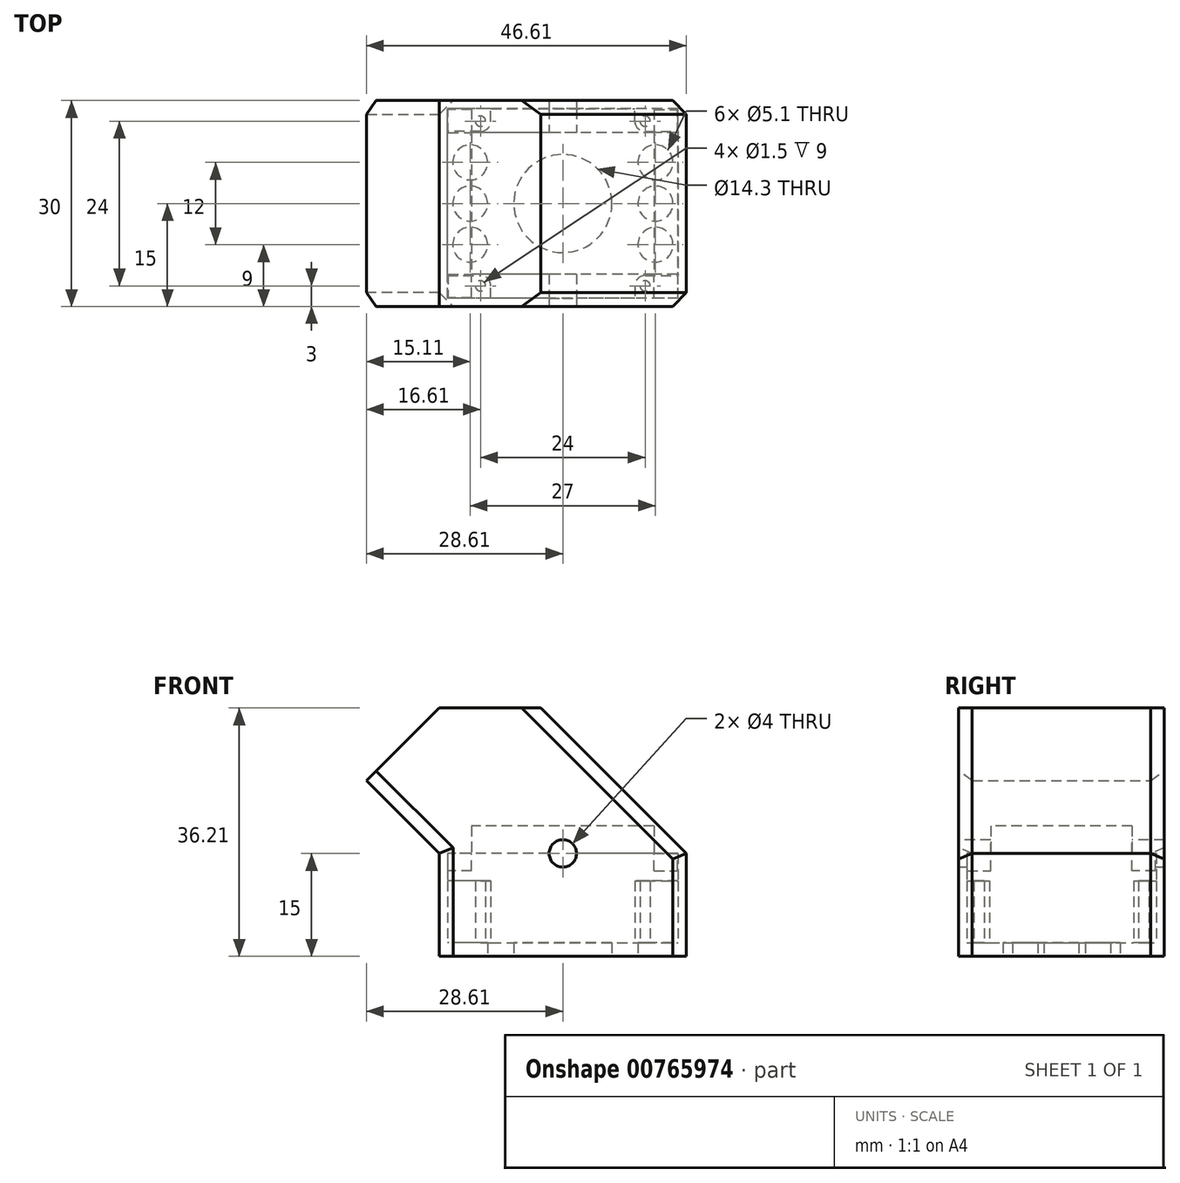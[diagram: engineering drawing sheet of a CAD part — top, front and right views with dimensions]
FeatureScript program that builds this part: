
annotation { "Feature Type Name" : "Feature", "Feature Type Description" : "" }
export const myFeature = defineFeature(function(context is Context, id is Id, definition is map)
    precondition{}
    {
        {
            var Q0;
            Q0=qCreatedBy(makeId("Top.planeOp"),FACE);
            var sketch = newSketch(context, id + "F0", { "sketchPlane" : qUnion([Q0])});
            skLineSegment(sketch, "E0.bottom", {"start": v(12, -12) * mm, "end": v(-12, -12) * mm, "construction": true});
            skLineSegment(sketch, "E0.top", {"start": v(12, 12) * mm, "end": v(-12, 12) * mm, "construction": true});
            skLineSegment(sketch, "E0.left", {"start": v(12, -12) * mm, "end": v(12, 12) * mm, "construction": true});
            skLineSegment(sketch, "E0.right", {"start": v(-12, -12) * mm, "end": v(-12, 12) * mm, "construction": true});
            skPoint(sketch, "E0.middle", {"position": v(0, 0) * mm});
            skCircle(sketch, "E1", {"center": v(-12, 12) * mm, "radius": 0.75 * mm});
            skCircle(sketch, "E2", {"center": v(-12, -12) * mm, "radius": 0.75 * mm});
            skCircle(sketch, "E3", {"center": v(12, -12) * mm, "radius": 0.75 * mm});
            skCircle(sketch, "E4", {"center": v(12, 12) * mm, "radius": 0.75 * mm});
            skCircle(sketch, "E5", {"center": v(0, 0) * mm, "radius": 7.15 * mm});
            skLineSegment(sketch, "E6", {"start": v(-13.5, 6) * mm, "end": v(-13.5, -6) * mm, "construction": true});
            skLineSegment(sketch, "E7", {"start": v(13.5, 6) * mm, "end": v(13.5, -6) * mm, "construction": true});
            skCircle(sketch, "E8", {"center": v(-13.5, 6) * mm, "radius": 2.55 * mm});
            skCircle(sketch, "E9", {"center": v(-13.5, 0) * mm, "radius": 2.55 * mm});
            skCircle(sketch, "E10", {"center": v(-13.5, -6) * mm, "radius": 2.55 * mm});
            skCircle(sketch, "E11", {"center": v(13.5, -6) * mm, "radius": 2.55 * mm});
            skCircle(sketch, "E12", {"center": v(13.5, 0) * mm, "radius": 2.55 * mm});
            skCircle(sketch, "E13", {"center": v(13.5, 6) * mm, "radius": 2.55 * mm});
            skLineSegment(sketch, "E14.bottom", {"start": v(15, -12.5) * mm, "end": v(-15, -12.5) * mm});
            skLineSegment(sketch, "E14.top", {"start": v(15, 12.5) * mm, "end": v(-15, 12.5) * mm});
            skLineSegment(sketch, "E14.left", {"start": v(15, -12.5) * mm, "end": v(15, 12.5) * mm});
            skLineSegment(sketch, "E14.right", {"start": v(-15, -12.5) * mm, "end": v(-15, 12.5) * mm});
            skSolve(sketch);
        }
        {
            var Q0;
            Q0=qCreatedBy(makeId("Top.planeOp"),FACE);
            var sketch = newSketch(context, id + "F1", { "sketchPlane" : qUnion([Q0])});
            skLineSegment(sketch, "E15.bottom", {"start": v(18, -15) * mm, "end": v(-18, -15) * mm});
            skLineSegment(sketch, "E15.top", {"start": v(18, 15) * mm, "end": v(-18, 15) * mm});
            skLineSegment(sketch, "E15.left", {"start": v(18, -15) * mm, "end": v(18, 15) * mm});
            skLineSegment(sketch, "E15.right", {"start": v(-18, -15) * mm, "end": v(-18, 15) * mm});
            skPoint(sketch, "E15.middle", {"position": v(0, 0) * mm});
            skCircle(sketch, "E16", {"center": v(0, 0) * mm, "radius": 7.15 * mm});
            skCircle(sketch, "E17", {"center": v(-13.5, 6) * mm, "radius": 2.55 * mm});
            skCircle(sketch, "E18", {"center": v(-13.5, 0) * mm, "radius": 2.55 * mm});
            skCircle(sketch, "E19", {"center": v(-13.5, -6) * mm, "radius": 2.55 * mm});
            skCircle(sketch, "E20", {"center": v(13.5, 6) * mm, "radius": 2.55 * mm});
            skCircle(sketch, "E21", {"center": v(13.5, 0) * mm, "radius": 2.55 * mm});
            skCircle(sketch, "E22", {"center": v(13.5, -6) * mm, "radius": 2.55 * mm});
            skSolve(sketch);
        }
        {
            var Q0;
            Q0=qSketchRegion(id+"F1",true);
            extrude(context, id + "F2", {"entities" : qUnion([Q0]), "depth" : 2 * mm, "offsetDistance" : 25 * mm});
        }
        {
            var Q0;
            Q0=makeQuery(id+"F2.opExtrude","CAP_FACE",FACE,{"disambiguationData":[OSD([sQuery(id+"F1.wireOp",EDGE,"E15.bottom"),sQuery(id+"F1.wireOp",EDGE,"E15.top"),sQuery(id+"F1.wireOp",EDGE,"E15.left"),sQuery(id+"F1.wireOp",EDGE,"E15.right"),sQuery(id+"F1.wireOp",EDGE,"E16"),sQuery(id+"F1.wireOp",EDGE,"E17"),sQuery(id+"F1.wireOp",EDGE,"E18"),sQuery(id+"F1.wireOp",EDGE,"E19"),sQuery(id+"F1.wireOp",EDGE,"E20"),sQuery(id+"F1.wireOp",EDGE,"E21"),sQuery(id+"F1.wireOp",EDGE,"E22")])],"isStart":false});
            var sketch = newSketch(context, id + "F3", { "sketchPlane" : qUnion([Q0])});
            skLineSegment(sketch, "E23.bottom", {"start": v(18, -15) * mm, "end": v(-18, -15) * mm});
            skLineSegment(sketch, "E23.top", {"start": v(18, 15) * mm, "end": v(-18, 15) * mm});
            skLineSegment(sketch, "E23.left", {"start": v(18, -15) * mm, "end": v(18, 15) * mm});
            skLineSegment(sketch, "E23.right", {"start": v(-18, -15) * mm, "end": v(-18, 15) * mm});
            skPoint(sketch, "E23.middle", {"position": v(0, 0) * mm});
            skLineSegment(sketch, "E24", {"start": v(-12, 10.5) * mm, "end": v(-16.8, 10.5) * mm});
            skLineSegment(sketch, "E25", {"start": v(-10.5, 12) * mm, "end": v(-10.5, 13.8) * mm});
            skLineSegment(sketch, "E26", {"start": v(-10.5, -13.8) * mm, "end": v(-10.5, -12) * mm});
            skLineSegment(sketch, "E27", {"start": v(-16.8, -10.5) * mm, "end": v(-12, -10.5) * mm});
            skLineSegment(sketch, "E28", {"start": v(10.5, -12) * mm, "end": v(10.5, -13.8) * mm});
            skLineSegment(sketch, "E29", {"start": v(12, -10.5) * mm, "end": v(16.8, -10.5) * mm});
            skLineSegment(sketch, "E30", {"start": v(10.5, 12) * mm, "end": v(10.5, 13.8) * mm});
            skLineSegment(sketch, "E31", {"start": v(12, 10.5) * mm, "end": v(16.8, 10.5) * mm});
            skArc(sketch, "E32", {"start": v(-12, 10.5) * mm, "mid": v(-10.94, 10.94) * mm, "end": v(-10.5, 12) * mm});
            skArc(sketch, "E33", {"start": v(10.5, 12) * mm, "mid": v(10.94, 10.94) * mm, "end": v(12, 10.5) * mm});
            skArc(sketch, "E34", {"start": v(12, -10.5) * mm, "mid": v(10.94, -10.94) * mm, "end": v(10.5, -12) * mm});
            skArc(sketch, "E35", {"start": v(-10.5, -12) * mm, "mid": v(-10.94, -10.94) * mm, "end": v(-12, -10.5) * mm});
            skLineSegment(sketch, "E36", {"start": v(-10.5, 13.8) * mm, "end": v(10.5, 13.8) * mm});
            skLineSegment(sketch, "E37", {"start": v(16.8, 10.5) * mm, "end": v(16.8, -10.5) * mm});
            skLineSegment(sketch, "E38", {"start": v(10.5, -13.8) * mm, "end": v(-10.5, -13.8) * mm});
            skLineSegment(sketch, "E39", {"start": v(-16.8, -10.5) * mm, "end": v(-16.8, 10.5) * mm});
            skCircle(sketch, "E40", {"center": v(-12, 12) * mm, "radius": 0.75 * mm});
            skCircle(sketch, "E41", {"center": v(12, 12) * mm, "radius": 0.75 * mm});
            skCircle(sketch, "E42", {"center": v(12, -12) * mm, "radius": 0.75 * mm});
            skCircle(sketch, "E43", {"center": v(-12, -12) * mm, "radius": 0.75 * mm});
            skSolve(sketch);
        }
        {
            var Q0;
            Q0=qSketchRegion(id+"F3",true);
            extrude(context, id + "F4", {"entities" : qUnion([Q0]), "operationType" : NewBodyOperationType.ADD, "depth" : 9 * mm, "offsetDistance" : 25 * mm});
        }
        {
            var Q0;
            Q0=makeQuery(id+"F4.opExtrude","CAP_FACE",FACE,{"disambiguationData":[OSD([sQuery(id+"F3.wireOp",EDGE,"E23.bottom"),sQuery(id+"F3.wireOp",EDGE,"E23.top"),sQuery(id+"F3.wireOp",EDGE,"E23.left"),sQuery(id+"F3.wireOp",EDGE,"E23.right"),sQuery(id+"F3.wireOp",EDGE,"E24"),sQuery(id+"F3.wireOp",EDGE,"E25"),sQuery(id+"F3.wireOp",EDGE,"E26"),sQuery(id+"F3.wireOp",EDGE,"E27"),sQuery(id+"F3.wireOp",EDGE,"E28"),sQuery(id+"F3.wireOp",EDGE,"E29"),sQuery(id+"F3.wireOp",EDGE,"E30"),sQuery(id+"F3.wireOp",EDGE,"E31"),sQuery(id+"F3.wireOp",EDGE,"E32"),sQuery(id+"F3.wireOp",EDGE,"E33"),sQuery(id+"F3.wireOp",EDGE,"E34"),sQuery(id+"F3.wireOp",EDGE,"E35"),sQuery(id+"F3.wireOp",EDGE,"E36"),sQuery(id+"F3.wireOp",EDGE,"E37"),sQuery(id+"F3.wireOp",EDGE,"E38"),sQuery(id+"F3.wireOp",EDGE,"E39"),sQuery(id+"F3.wireOp",EDGE,"E40"),sQuery(id+"F3.wireOp",EDGE,"E41"),sQuery(id+"F3.wireOp",EDGE,"E42"),sQuery(id+"F3.wireOp",EDGE,"E43")])],"isStart":false});
            var sketch = newSketch(context, id + "F5", { "sketchPlane" : qUnion([Q0])});
            skLineSegment(sketch, "E44.bottom", {"start": v(18, -15) * mm, "end": v(-18, -15) * mm});
            skLineSegment(sketch, "E44.top", {"start": v(18, 15) * mm, "end": v(-18, 15) * mm});
            skLineSegment(sketch, "E44.left", {"start": v(18, -15) * mm, "end": v(18, 15) * mm});
            skLineSegment(sketch, "E44.right", {"start": v(-18, -15) * mm, "end": v(-18, 15) * mm});
            skPoint(sketch, "E44.middle", {"position": v(0, 0) * mm});
            skLineSegment(sketch, "E45.bottom", {"start": v(16.8, -13.8) * mm, "end": v(-16.8, -13.8) * mm});
            skLineSegment(sketch, "E45.top", {"start": v(16.8, 13.8) * mm, "end": v(-16.8, 13.8) * mm});
            skLineSegment(sketch, "E45.left", {"start": v(16.8, -13.8) * mm, "end": v(16.8, 13.8) * mm});
            skLineSegment(sketch, "E45.right", {"start": v(-16.8, -13.8) * mm, "end": v(-16.8, 13.8) * mm});
            skSolve(sketch);
        }
        {
            var Q0;
            Q0=qSketchRegion(id+"F5",true);
            extrude(context, id + "F6", {"entities" : qUnion([Q0]), "operationType" : NewBodyOperationType.ADD, "depth" : 4 * mm, "offsetDistance" : 25 * mm});
        }
        {
            var Q0;
            Q0=makeQuery(id+"F6.opExtrude","CAP_FACE",FACE,{"disambiguationData":[OSD([sQuery(id+"F5.wireOp",EDGE,"E44.bottom"),sQuery(id+"F5.wireOp",EDGE,"E44.top"),sQuery(id+"F5.wireOp",EDGE,"E44.left"),sQuery(id+"F5.wireOp",EDGE,"E44.right"),sQuery(id+"F5.wireOp",EDGE,"E45.bottom"),sQuery(id+"F5.wireOp",EDGE,"E45.top"),sQuery(id+"F5.wireOp",EDGE,"E45.left"),sQuery(id+"F5.wireOp",EDGE,"E45.right")])],"isStart":false});
            var sketch = newSketch(context, id + "F7", { "sketchPlane" : qUnion([Q0])});
            skLineSegment(sketch, "E46.bottom", {"start": v(18, -15) * mm, "end": v(-18, -15) * mm});
            skLineSegment(sketch, "E46.top", {"start": v(18, 15) * mm, "end": v(-18, 15) * mm});
            skLineSegment(sketch, "E46.left", {"start": v(18, -15) * mm, "end": v(18, 15) * mm});
            skLineSegment(sketch, "E46.right", {"start": v(-18, -15) * mm, "end": v(-18, 15) * mm});
            skPoint(sketch, "E46.middle", {"position": v(0, 0) * mm});
            skLineSegment(sketch, "E47.top", {"start": v(-16.8, 10.3) * mm, "end": v(-13.3, 10.3) * mm});
            skLineSegment(sketch, "E47.right", {"start": v(-13.3, 13.8) * mm, "end": v(-13.3, 10.3) * mm});
            skLineSegment(sketch, "E48.top", {"start": v(16.8, 10.3) * mm, "end": v(13.3, 10.3) * mm});
            skLineSegment(sketch, "E48.right", {"start": v(13.3, 13.8) * mm, "end": v(13.3, 10.3) * mm});
            skLineSegment(sketch, "E49.top", {"start": v(16.8, -10.3) * mm, "end": v(13.3, -10.3) * mm});
            skLineSegment(sketch, "E49.right", {"start": v(13.3, -13.8) * mm, "end": v(13.3, -10.3) * mm});
            skLineSegment(sketch, "E50.top", {"start": v(-16.8, -10.3) * mm, "end": v(-13.3, -10.3) * mm});
            skLineSegment(sketch, "E50.right", {"start": v(-13.3, -13.8) * mm, "end": v(-13.3, -10.3) * mm});
            skLineSegment(sketch, "E51", {"start": v(-16.8, -10.3) * mm, "end": v(-16.8, 10.3) * mm});
            skLineSegment(sketch, "E52", {"start": v(-13.3, 13.8) * mm, "end": v(13.3, 13.8) * mm});
            skLineSegment(sketch, "E53", {"start": v(16.8, 10.3) * mm, "end": v(16.8, -10.3) * mm});
            skLineSegment(sketch, "E54", {"start": v(13.3, -13.8) * mm, "end": v(-13.3, -13.8) * mm});
            skSolve(sketch);
        }
        {
            var Q0;
            Q0=qSketchRegion(id+"F7",true);
            extrude(context, id + "F8", {"entities" : qUnion([Q0]), "depth" : 4 * mm, "offsetDistance" : 25 * mm});
        }
        {
            var Q0;
            Q0=makeQuery(id+"F8.opExtrude","CAP_FACE",FACE,{"disambiguationData":[OSD([sQuery(id+"F7.wireOp",EDGE,"E46.bottom"),sQuery(id+"F7.wireOp",EDGE,"E46.top"),sQuery(id+"F7.wireOp",EDGE,"E46.left"),sQuery(id+"F7.wireOp",EDGE,"E46.right"),sQuery(id+"F7.wireOp",EDGE,"E47.top"),sQuery(id+"F7.wireOp",EDGE,"E47.right"),sQuery(id+"F7.wireOp",EDGE,"E48.top"),sQuery(id+"F7.wireOp",EDGE,"E48.right"),sQuery(id+"F7.wireOp",EDGE,"E49.top"),sQuery(id+"F7.wireOp",EDGE,"E49.right"),sQuery(id+"F7.wireOp",EDGE,"E50.top"),sQuery(id+"F7.wireOp",EDGE,"E50.right"),sQuery(id+"F7.wireOp",EDGE,"E51"),sQuery(id+"F7.wireOp",EDGE,"E52"),sQuery(id+"F7.wireOp",EDGE,"E53"),sQuery(id+"F7.wireOp",EDGE,"E54")])],"isStart":true});
            var sketch = newSketch(context, id + "F9", { "sketchPlane" : qUnion([Q0])});
            skLineSegment(sketch, "E55.bottom", {"start": v(-13.3, -10.3) * mm, "end": v(-16.72, -10.3) * mm});
            skLineSegment(sketch, "E55.top", {"start": v(-13.3, -13.72) * mm, "end": v(-16.72, -13.72) * mm});
            skLineSegment(sketch, "E55.left", {"start": v(-13.3, -10.3) * mm, "end": v(-13.3, -13.72) * mm});
            skLineSegment(sketch, "E55.right", {"start": v(-16.72, -10.3) * mm, "end": v(-16.72, -13.72) * mm});
            skLineSegment(sketch, "E56.bottom", {"start": v(13.3, -10.3) * mm, "end": v(16.72, -10.3) * mm});
            skLineSegment(sketch, "E56.top", {"start": v(13.3, -13.72) * mm, "end": v(16.72, -13.72) * mm});
            skLineSegment(sketch, "E56.left", {"start": v(13.3, -10.3) * mm, "end": v(13.3, -13.72) * mm});
            skLineSegment(sketch, "E56.right", {"start": v(16.72, -10.3) * mm, "end": v(16.72, -13.72) * mm});
            skLineSegment(sketch, "E57.bottom", {"start": v(-13.3, 10.3) * mm, "end": v(-16.72, 10.3) * mm});
            skLineSegment(sketch, "E57.top", {"start": v(-13.3, 13.72) * mm, "end": v(-16.72, 13.72) * mm});
            skLineSegment(sketch, "E57.left", {"start": v(-13.3, 10.3) * mm, "end": v(-13.3, 13.72) * mm});
            skLineSegment(sketch, "E57.right", {"start": v(-16.72, 10.3) * mm, "end": v(-16.72, 13.72) * mm});
            skLineSegment(sketch, "E58.bottom", {"start": v(13.3, 10.3) * mm, "end": v(16.72, 10.3) * mm});
            skLineSegment(sketch, "E58.top", {"start": v(13.3, 13.72) * mm, "end": v(16.72, 13.72) * mm});
            skLineSegment(sketch, "E58.left", {"start": v(13.3, 10.3) * mm, "end": v(13.3, 13.72) * mm});
            skLineSegment(sketch, "E58.right", {"start": v(16.72, 10.3) * mm, "end": v(16.72, 13.72) * mm});
            skSolve(sketch);
        }
        {
            var Q0;
            Q0=qSketchRegion(id+"F9",true);
            extrude(context, id + "F10", {"entities" : qUnion([Q0]), "operationType" : NewBodyOperationType.ADD, "depth" : 2.5 * mm, "offsetDistance" : 25 * mm});
        }
        {
            var Q0;
            Q0=makeQuery(id+"F8.opExtrude","CAP_FACE",FACE,{"disambiguationData":[OSD([sQuery(id+"F7.wireOp",EDGE,"E46.bottom"),sQuery(id+"F7.wireOp",EDGE,"E46.top"),sQuery(id+"F7.wireOp",EDGE,"E46.left"),sQuery(id+"F7.wireOp",EDGE,"E46.right"),sQuery(id+"F7.wireOp",EDGE,"E47.top"),sQuery(id+"F7.wireOp",EDGE,"E47.right"),sQuery(id+"F7.wireOp",EDGE,"E48.top"),sQuery(id+"F7.wireOp",EDGE,"E48.right"),sQuery(id+"F7.wireOp",EDGE,"E49.top"),sQuery(id+"F7.wireOp",EDGE,"E49.right"),sQuery(id+"F7.wireOp",EDGE,"E50.top"),sQuery(id+"F7.wireOp",EDGE,"E50.right"),sQuery(id+"F7.wireOp",EDGE,"E51"),sQuery(id+"F7.wireOp",EDGE,"E52"),sQuery(id+"F7.wireOp",EDGE,"E53"),sQuery(id+"F7.wireOp",EDGE,"E54")])],"isStart":false});
            var sketch = newSketch(context, id + "F11", { "sketchPlane" : qUnion([Q0])});
            skLineSegment(sketch, "E59.bottom", {"start": v(18, -15) * mm, "end": v(-18, -15) * mm});
            skLineSegment(sketch, "E59.top", {"start": v(18, 15) * mm, "end": v(-18, 15) * mm});
            skLineSegment(sketch, "E59.left", {"start": v(18, -15) * mm, "end": v(18, 15) * mm});
            skLineSegment(sketch, "E59.right", {"start": v(-18, -15) * mm, "end": v(-18, 15) * mm});
            skPoint(sketch, "E59.middle", {"position": v(0, 0) * mm});
            skSolve(sketch);
        }
        {
            var Q0;
            Q0=qSketchRegion(id+"F11",true);
            extrude(context, id + "F12", {"entities" : qUnion([Q0]), "operationType" : NewBodyOperationType.ADD, "depth" : 2 * mm, "offsetDistance" : 25 * mm});
        }
        {
            var Q0;
            Q0=qCreatedBy(makeId("Front.planeOp"),FACE);
            var sketch = newSketch(context, id + "F13", { "sketchPlane" : qUnion([Q0])});
            skLineSegment(sketch, "E60", {"start": v(0, -28.52) * mm, "end": v(-155.56, -184.08) * mm, "construction": true});
            skLineSegment(sketch, "E61", {"start": v(0, -28.52) * mm, "end": v(155.56, -184.08) * mm, "construction": true});
            skLineSegment(sketch, "E62", {"start": v(-10.6, 43.6) * mm, "end": v(22.27, 10.73) * mm, "construction": true});
            skLineSegment(sketch, "E63", {"start": v(-10.6, 43.6) * mm, "end": v(-30.76, 23.45) * mm, "construction": true});
            skLineSegment(sketch, "E64", {"start": v(-18, 36.21) * mm, "end": v(-28.6, 25.6) * mm});
            skLineSegment(sketch, "E65", {"start": v(-28.6, 25.6) * mm, "end": v(-18, 15) * mm});
            skLineSegment(sketch, "E66", {"start": v(-18, 15) * mm, "end": v(18, 15) * mm});
            skLineSegment(sketch, "E67", {"start": v(18, 15) * mm, "end": v(-3.21, 36.21) * mm});
            skLineSegment(sketch, "E68", {"start": v(-3.21, 36.21) * mm, "end": v(-18, 36.21) * mm});
            skSolve(sketch);
        }
        {
            var Q0;
            Q0=qSketchRegion(id+"F13",true);
            extrude(context, id + "F14", {"entities" : qUnion([Q0]), "operationType" : NewBodyOperationType.ADD, "endBound" : BoundingType.SYMMETRIC, "depth" : 30 * mm, "offsetDistance" : 25 * mm});
        }
        {
            var Q0;
            Q0=qCreatedBy(makeId("Front.planeOp"),FACE);
            var sketch = newSketch(context, id + "F15", { "sketchPlane" : qUnion([Q0])});
            skLineSegment(sketch, "E69", {"start": v(12, 21) * mm, "end": v(18, 15) * mm});
            skLineSegment(sketch, "E70", {"start": v(18, 15) * mm, "end": v(18, 21) * mm});
            skLineSegment(sketch, "E71", {"start": v(18, 21) * mm, "end": v(12, 21) * mm});
            skSolve(sketch);
        }
        {
            var Q0;
            Q0=qSketchRegion(id+"F15",true);
            extrude(context, id + "F16", {"entities" : qUnion([Q0]), "operationType" : NewBodyOperationType.REMOVE, "endBound" : BoundingType.SYMMETRIC, "oppositeDirection" : true, "depth" : 36 * mm, "offsetDistance" : 25 * mm});
        }
        {
            var Q0;
            Q0=makeQuery(id+"F14.boolean.opBoolean","MERGE",FACE,{"derivedFrom":[makeQuery(id+"F8.opExtrude","CAP_FACE",FACE,{"disambiguationData":[OSD([sQuery(id+"F7.wireOp",EDGE,"E46.bottom"),sQuery(id+"F7.wireOp",EDGE,"E46.top"),sQuery(id+"F7.wireOp",EDGE,"E46.left"),sQuery(id+"F7.wireOp",EDGE,"E46.right"),sQuery(id+"F7.wireOp",EDGE,"E47.top"),sQuery(id+"F7.wireOp",EDGE,"E47.right"),sQuery(id+"F7.wireOp",EDGE,"E48.top"),sQuery(id+"F7.wireOp",EDGE,"E48.right"),sQuery(id+"F7.wireOp",EDGE,"E49.top"),sQuery(id+"F7.wireOp",EDGE,"E49.right"),sQuery(id+"F7.wireOp",EDGE,"E50.top"),sQuery(id+"F7.wireOp",EDGE,"E50.right"),sQuery(id+"F7.wireOp",EDGE,"E51"),sQuery(id+"F7.wireOp",EDGE,"E52"),sQuery(id+"F7.wireOp",EDGE,"E53"),sQuery(id+"F7.wireOp",EDGE,"E54")])],"isStart":true}),makeQuery(id+"F14.opExtrude","SWEPT_FACE",FACE,{"disambiguationData":[OSD([sQuery(id+"F13.wireOp",EDGE,"vBC8PzHA-Ugvo-uK9Q-XWij-d8i4ykoGp8h1")])]})]});
            var sketch = newSketch(context, id + "F17", { "sketchPlane" : qUnion([Q0])});
            skLineSegment(sketch, "E72.bottom", {"start": v(13.3, -10.3) * mm, "end": v(-13.3, -10.3) * mm});
            skLineSegment(sketch, "E72.top", {"start": v(13.3, 10.3) * mm, "end": v(-13.3, 10.3) * mm});
            skLineSegment(sketch, "E72.left", {"start": v(13.3, -10.3) * mm, "end": v(13.3, 10.3) * mm});
            skLineSegment(sketch, "E72.right", {"start": v(-13.3, -10.3) * mm, "end": v(-13.3, 10.3) * mm});
            skPoint(sketch, "E72.middle", {"position": v(0, 0) * mm});
            skSolve(sketch);
        }
        {
            var Q0;
            Q0=qSketchRegion(id+"F17",true);
            extrude(context, id + "F18", {"entities" : qUnion([Q0]), "operationType" : NewBodyOperationType.REMOVE, "oppositeDirection" : true, "depth" : 4 * mm, "offsetDistance" : 25 * mm});
        }
        {
            var Q0;
            Q0=qCreatedBy(makeId("Front.planeOp"),FACE);
            var sketch = newSketch(context, id + "F19", { "sketchPlane" : qUnion([Q0])});
            skCircle(sketch, "E73", {"center": v(0, 15) * mm, "radius": 2 * mm});
            skSolve(sketch);
        }
        {
            var Q0;
            Q0=qSketchRegion(id+"F19",true);
            extrude(context, id + "F20", {"entities" : qUnion([Q0]), "operationType" : NewBodyOperationType.REMOVE, "endBound" : BoundingType.SYMMETRIC, "oppositeDirection" : true, "depth" : 2000 * mm, "offsetDistance" : 25 * mm});
        }
        {
            var Q0;
            Q0=makeQuery(id+"F6.boolean.opBoolean","MERGE",EDGE,{"derivedFrom":[makeQuery(id+"F4.boolean.opBoolean","MERGE",EDGE,{"derivedFrom":[makeQuery(id+"F2.opExtrude","SWEPT_EDGE",EDGE,{"disambiguationData":[OSD([sQuery(id+"F1.wireOp",EDGE,"E15.top"),sQuery(id+"F1.wireOp",EDGE,"E15.right")])]}),makeQuery(id+"F4.opExtrude","SWEPT_EDGE",EDGE,{"disambiguationData":[OSD([sQuery(id+"F3.wireOp",EDGE,"E23.top"),sQuery(id+"F3.wireOp",EDGE,"E23.right")])]})]}),makeQuery(id+"F6.opExtrude","SWEPT_EDGE",EDGE,{"disambiguationData":[OSD([sQuery(id+"F5.wireOp",EDGE,"E44.top"),sQuery(id+"F5.wireOp",EDGE,"E44.right")])]})]});
            var Q1;
            Q1=makeQuery(id+"F12.boolean.opBoolean","MERGE",EDGE,{"derivedFrom":[makeQuery(id+"F8.opExtrude","SWEPT_EDGE",EDGE,{"disambiguationData":[OSD([sQuery(id+"F7.wireOp",EDGE,"E46.top"),sQuery(id+"F7.wireOp",EDGE,"E46.right")])]}),makeQuery(id+"F12.opExtrude","SWEPT_EDGE",EDGE,{"disambiguationData":[OSD([sQuery(id+"F11.wireOp",EDGE,"E59.top"),sQuery(id+"F11.wireOp",EDGE,"E59.right")])]})]});
            var Q2;
            Q2=makeQuery(id+"F6.boolean.opBoolean","MERGE",EDGE,{"derivedFrom":[makeQuery(id+"F4.boolean.opBoolean","MERGE",EDGE,{"derivedFrom":[makeQuery(id+"F2.opExtrude","SWEPT_EDGE",EDGE,{"disambiguationData":[OSD([sQuery(id+"F1.wireOp",EDGE,"E15.bottom"),sQuery(id+"F1.wireOp",EDGE,"E15.right")])]}),makeQuery(id+"F4.opExtrude","SWEPT_EDGE",EDGE,{"disambiguationData":[OSD([sQuery(id+"F3.wireOp",EDGE,"E23.bottom"),sQuery(id+"F3.wireOp",EDGE,"E23.right")])]})]}),makeQuery(id+"F6.opExtrude","SWEPT_EDGE",EDGE,{"disambiguationData":[OSD([sQuery(id+"F5.wireOp",EDGE,"E44.bottom"),sQuery(id+"F5.wireOp",EDGE,"E44.right")])]})]});
            var Q3;
            Q3=makeQuery(id+"F12.boolean.opBoolean","MERGE",EDGE,{"derivedFrom":[makeQuery(id+"F8.opExtrude","SWEPT_EDGE",EDGE,{"disambiguationData":[OSD([sQuery(id+"F7.wireOp",EDGE,"E46.bottom"),sQuery(id+"F7.wireOp",EDGE,"E46.right")])]}),makeQuery(id+"F12.opExtrude","SWEPT_EDGE",EDGE,{"disambiguationData":[OSD([sQuery(id+"F11.wireOp",EDGE,"E59.bottom"),sQuery(id+"F11.wireOp",EDGE,"E59.right")])]})]});
            var Q4;
            Q4=makeQuery(id+"F6.boolean.opBoolean","MERGE",EDGE,{"derivedFrom":[makeQuery(id+"F4.boolean.opBoolean","MERGE",EDGE,{"derivedFrom":[makeQuery(id+"F2.opExtrude","SWEPT_EDGE",EDGE,{"disambiguationData":[OSD([sQuery(id+"F1.wireOp",EDGE,"E15.bottom"),sQuery(id+"F1.wireOp",EDGE,"E15.left")])]}),makeQuery(id+"F4.opExtrude","SWEPT_EDGE",EDGE,{"disambiguationData":[OSD([sQuery(id+"F3.wireOp",EDGE,"E23.bottom"),sQuery(id+"F3.wireOp",EDGE,"E23.left")])]})]}),makeQuery(id+"F6.opExtrude","SWEPT_EDGE",EDGE,{"disambiguationData":[OSD([sQuery(id+"F5.wireOp",EDGE,"E44.bottom"),sQuery(id+"F5.wireOp",EDGE,"E44.left")])]})]});
            var Q5;
            Q5=makeQuery(id+"F12.boolean.opBoolean","MERGE",EDGE,{"derivedFrom":[makeQuery(id+"F8.opExtrude","SWEPT_EDGE",EDGE,{"disambiguationData":[OSD([sQuery(id+"F7.wireOp",EDGE,"E46.bottom"),sQuery(id+"F7.wireOp",EDGE,"E46.left")])]}),makeQuery(id+"F12.opExtrude","SWEPT_EDGE",EDGE,{"disambiguationData":[OSD([sQuery(id+"F11.wireOp",EDGE,"E59.bottom"),sQuery(id+"F11.wireOp",EDGE,"E59.left")])]})]});
            var Q6;
            Q6=makeQuery(id+"F6.boolean.opBoolean","MERGE",EDGE,{"derivedFrom":[makeQuery(id+"F4.boolean.opBoolean","MERGE",EDGE,{"derivedFrom":[makeQuery(id+"F2.opExtrude","SWEPT_EDGE",EDGE,{"disambiguationData":[OSD([sQuery(id+"F1.wireOp",EDGE,"E15.top"),sQuery(id+"F1.wireOp",EDGE,"E15.left")])]}),makeQuery(id+"F4.opExtrude","SWEPT_EDGE",EDGE,{"disambiguationData":[OSD([sQuery(id+"F3.wireOp",EDGE,"E23.top"),sQuery(id+"F3.wireOp",EDGE,"E23.left")])]})]}),makeQuery(id+"F6.opExtrude","SWEPT_EDGE",EDGE,{"disambiguationData":[OSD([sQuery(id+"F5.wireOp",EDGE,"E44.top"),sQuery(id+"F5.wireOp",EDGE,"E44.left")])]})]});
            var Q7;
            Q7=makeQuery(id+"F12.boolean.opBoolean","MERGE",EDGE,{"derivedFrom":[makeQuery(id+"F8.opExtrude","SWEPT_EDGE",EDGE,{"disambiguationData":[OSD([sQuery(id+"F7.wireOp",EDGE,"E46.top"),sQuery(id+"F7.wireOp",EDGE,"E46.left")])]}),makeQuery(id+"F12.opExtrude","SWEPT_EDGE",EDGE,{"disambiguationData":[OSD([sQuery(id+"F11.wireOp",EDGE,"E59.top"),sQuery(id+"F11.wireOp",EDGE,"E59.left")])]})]});
            var Q8;
            Q8=makeQuery(id+"F16.boolean.opBoolean","MERGE",EDGE,{"derivedFrom":[makeQuery(id+"F14.opExtrude","CAP_EDGE",EDGE,{"disambiguationData":[OSD([sQuery(id+"F13.wireOp",EDGE,"DselsPWe-ErCp-aK2G-s9op-LOdKJn8xO6a4")])],"isStart":false})],"fromTools":[makeQuery(id+"F16.opExtrude","CAP_EDGE",EDGE,{"disambiguationData":[OSD([sQuery(id+"F15.wireOp",EDGE,"E69")])],"isStart":true})]});
            var Q9;
            Q9=makeQuery(id+"F14.opExtrude","CAP_EDGE",EDGE,{"disambiguationData":[OSD([sQuery(id+"F13.wireOp",EDGE,"3OIEeoqU-DmZ9-Cm3O-2OrO-ZmVaJZFvDNaF")])],"isStart":false});
            var Q10;
            Q10=makeQuery(id+"F14.opExtrude","CAP_EDGE",EDGE,{"disambiguationData":[OSD([sQuery(id+"F13.wireOp",EDGE,"3OIEeoqU-DmZ9-Cm3O-2OrO-ZmVaJZFvDNaF")])],"isStart":true});
            var Q11;
            Q11=makeQuery(id+"F16.boolean.opBoolean","MERGE",EDGE,{"derivedFrom":[makeQuery(id+"F14.opExtrude","CAP_EDGE",EDGE,{"disambiguationData":[OSD([sQuery(id+"F13.wireOp",EDGE,"DselsPWe-ErCp-aK2G-s9op-LOdKJn8xO6a4")])],"isStart":true})],"fromTools":[makeQuery(id+"F16.opExtrude","CAP_EDGE",EDGE,{"disambiguationData":[OSD([sQuery(id+"F15.wireOp",EDGE,"E69")])],"isStart":false})]});
            var Q12;
            Q12=makeQuery(id+"F14.opExtrude","CAP_EDGE",EDGE,{"disambiguationData":[OSD([sQuery(id+"F13.wireOp",EDGE,"E65")])],"isStart":false});
            var Q13;
            Q13=makeQuery(id+"F14.opExtrude","CAP_EDGE",EDGE,{"disambiguationData":[OSD([sQuery(id+"F13.wireOp",EDGE,"E65")])],"isStart":true});
            var Q14;
            Q14=makeQuery(id+"F16.boolean.opBoolean","INTERSECT",EDGE,{"derivedFrom":[makeQuery(id+"F14.boolean.opBoolean","MERGE",FACE,{"derivedFrom":[makeQuery(id+"F12.boolean.opBoolean","MERGE",FACE,{"derivedFrom":[makeQuery(id+"F8.opExtrude","SWEPT_FACE",FACE,{"disambiguationData":[OSD([sQuery(id+"F7.wireOp",EDGE,"E46.top")])]}),makeQuery(id+"F12.opExtrude","SWEPT_FACE",FACE,{"disambiguationData":[OSD([sQuery(id+"F11.wireOp",EDGE,"E59.top")])]})]}),makeQuery(id+"F14.opExtrude","CAP_FACE",FACE,{"disambiguationData":[OSD([sQuery(id+"F13.wireOp",EDGE,"E64"),sQuery(id+"F13.wireOp",EDGE,"E65"),sQuery(id+"F13.wireOp",EDGE,"E66"),sQuery(id+"F13.wireOp",EDGE,"E67"),sQuery(id+"F13.wireOp",EDGE,"E68")])],"isStart":true})]}),makeQuery(id+"F16.opExtrude","SWEPT_FACE",FACE,{"disambiguationData":[OSD([sQuery(id+"F15.wireOp",EDGE,"E69")])]})]});
            var Q15;
            Q15=makeQuery(id+"F16.boolean.opBoolean","INTERSECT",EDGE,{"derivedFrom":[makeQuery(id+"F14.boolean.opBoolean","MERGE",FACE,{"derivedFrom":[makeQuery(id+"F12.boolean.opBoolean","MERGE",FACE,{"derivedFrom":[makeQuery(id+"F8.opExtrude","SWEPT_FACE",FACE,{"disambiguationData":[OSD([sQuery(id+"F7.wireOp",EDGE,"E46.bottom")])]}),makeQuery(id+"F12.opExtrude","SWEPT_FACE",FACE,{"disambiguationData":[OSD([sQuery(id+"F11.wireOp",EDGE,"E59.bottom")])]})]}),makeQuery(id+"F14.opExtrude","CAP_FACE",FACE,{"disambiguationData":[OSD([sQuery(id+"F13.wireOp",EDGE,"E64"),sQuery(id+"F13.wireOp",EDGE,"E65"),sQuery(id+"F13.wireOp",EDGE,"E66"),sQuery(id+"F13.wireOp",EDGE,"E67"),sQuery(id+"F13.wireOp",EDGE,"E68")])],"isStart":false})]}),makeQuery(id+"F16.opExtrude","SWEPT_FACE",FACE,{"disambiguationData":[OSD([sQuery(id+"F15.wireOp",EDGE,"E69")])]})]});
            chamfer(context, id + "F21", {"entities" : qUnion([Q0, Q1, Q2, Q3, Q4, Q5, Q6, Q7, Q8, Q9, Q10, Q11, Q12, Q13, Q14, Q15]), "width" : 2 * mm, "tangentPropagation" : true});
        }
    });
